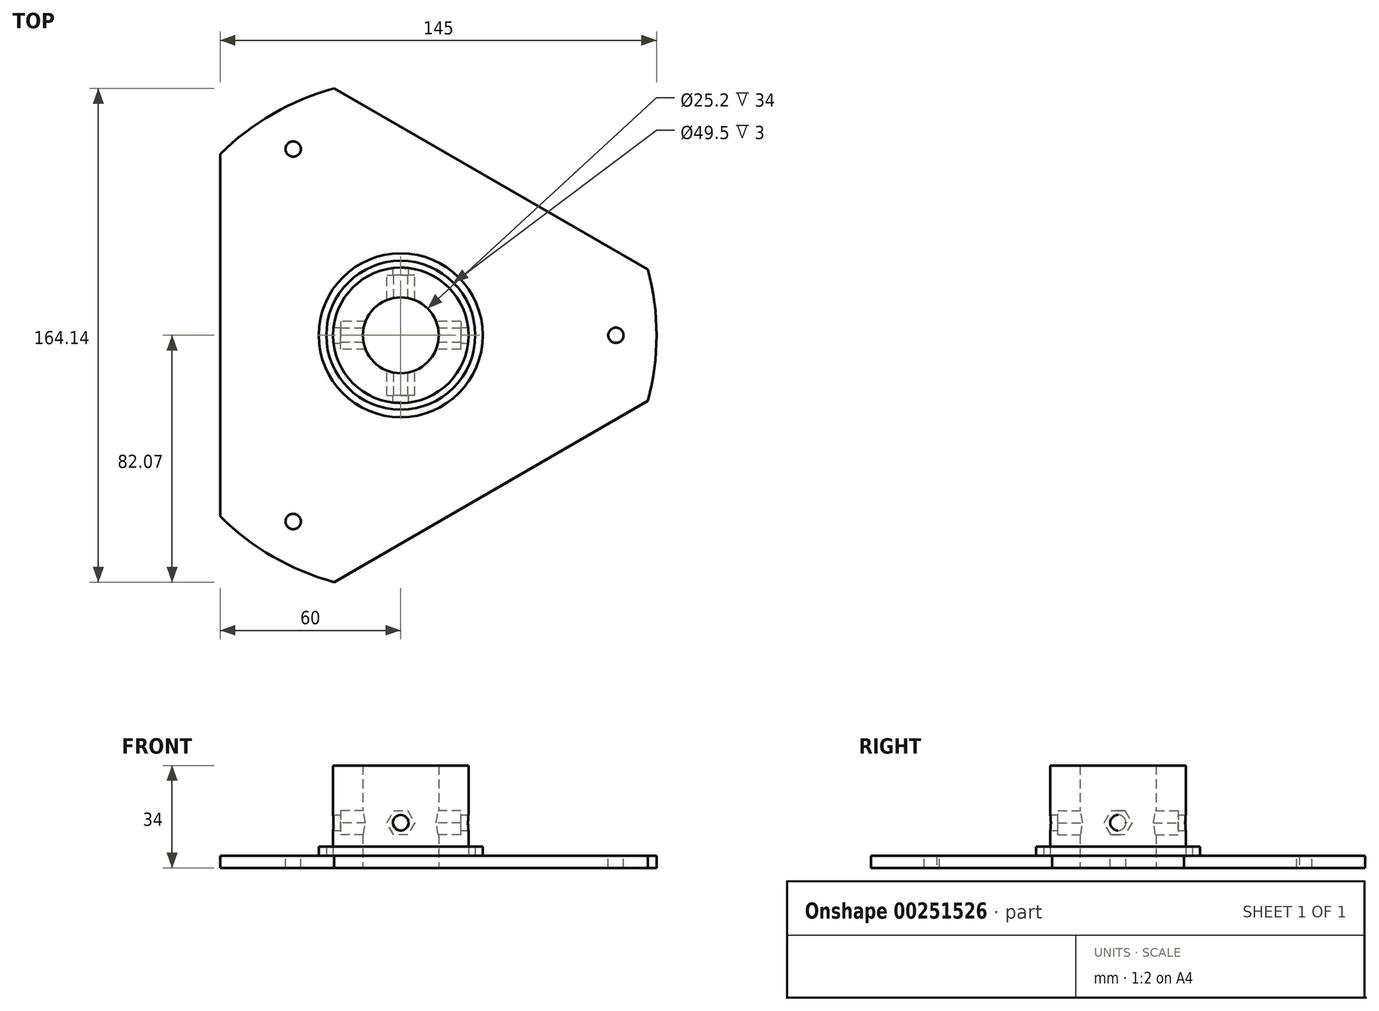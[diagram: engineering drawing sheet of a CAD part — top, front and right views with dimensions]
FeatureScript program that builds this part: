
annotation { "Feature Type Name" : "Feature", "Feature Type Description" : "" }
export const myFeature = defineFeature(function(context is Context, id is Id, definition is map)
    precondition{}
    {
        {
            var Q0;
            Q0=qCreatedBy(makeId("Top.planeOp"),FACE);
            var sketch = newSketch(context, id + "F0", { "sketchPlane" : qUnion([Q0])});
            skCircle(sketch, "E0", {"center": v(0, 0) * mm, "radius": 85 * mm});
            skCircle(sketch, "E1.cCircle", {"center": v(0, 0) * mm, "radius": 60 * mm, "construction": true});
            skLineSegment(sketch, "E1.0", {"start": v(120, 0) * mm, "end": v(-60, -103.92) * mm});
            skLineSegment(sketch, "E1.1", {"start": v(-60, -103.92) * mm, "end": v(-60, 103.92) * mm});
            skLineSegment(sketch, "E1.2", {"start": v(-60, 103.92) * mm, "end": v(120, 0) * mm});
            skPoint(sketch, "E1.0.midPoint", {"position": v(30, -51.96) * mm});
            skSolve(sketch);
        }
        {
            var Q0;
            {var subQ1=sQuery(id+"F0.wireOp",EDGE,"E0");var subQ4=sQuery(id+"F0.wireOp",EDGE,"E1.2");var subQ9=makeQuery(id+"F0.imprint","INTERSECT",VERTEX,{"disambiguationData":[OD(0.0)],"derivedFrom":[subQ1,subQ4]});Q0=makeQuery(id+"F0.imprint","IMPRINT",FACE,{"disambiguationData":[TD([[makeQuery(id+"F0.imprint","IMPRINT",EDGE,{"disambiguationData":[TD([[subQ9,-1.0]])],"derivedFrom":subQ1}),1.0]])]});}
            extrude(context, id + "F1", {"entities" : qUnion([Q0]), "depth" : 4 * mm});
        }
        {
            var Q0;
            Q0=makeQuery(id+"F1.opExtrude","CAP_FACE",FACE,{"disambiguationData":[OSD([sQuery(id+"F0.wireOp",EDGE,"E0"),sQuery(id+"F0.wireOp",EDGE,"E1.0"),sQuery(id+"F0.wireOp",EDGE,"E1.1"),sQuery(id+"F0.wireOp",EDGE,"E1.2")])],"isStart":false});
            var sketch = newSketch(context, id + "F2", { "sketchPlane" : qUnion([Q0])});
            skCircle(sketch, "E2", {"center": v(0, 0) * mm, "radius": 71.5 * mm});
            skLineSegment(sketch, "E3", {"start": v(0, 0) * mm, "end": v(118.31, 0) * mm, "construction": true});
            skCircle(sketch, "E4", {"center": v(71.5, 0) * mm, "radius": 2.55 * mm});
            skCircle(sketch, "E5.1.0", {"center": v(-35.75, 61.92) * mm, "radius": 2.55 * mm});
            skCircle(sketch, "E5.2.0", {"center": v(-35.75, -61.92) * mm, "radius": 2.55 * mm});
            skSolve(sketch);
        }
        {
            var Q0;
            {var subQ0=sQuery(id+"F2.wireOp",EDGE,"E4");var subQ1=sQuery(id+"F2.wireOp",EDGE,"E2");var subQ2=makeQuery(id+"F2.imprint","INTERSECT",VERTEX,{"disambiguationData":[OD(0.0)],"derivedFrom":[subQ1,subQ0]});Q0=makeQuery(id+"F2.imprint","IMPRINT",FACE,{"disambiguationData":[TD([[makeQuery(id+"F2.imprint","IMPRINT",EDGE,{"disambiguationData":[TD([[subQ2,1.0]])],"derivedFrom":subQ1}),1.0]])]});}
            var Q1;
            {var subQ0=sQuery(id+"F2.wireOp",EDGE,"E4");var subQ1=sQuery(id+"F2.wireOp",EDGE,"E2");var subQ2=makeQuery(id+"F2.imprint","INTERSECT",VERTEX,{"disambiguationData":[OD(0.0)],"derivedFrom":[subQ1,subQ0]});Q1=makeQuery(id+"F2.imprint","IMPRINT",FACE,{"disambiguationData":[TD([[makeQuery(id+"F2.imprint","IMPRINT",EDGE,{"disambiguationData":[TD([[subQ2,1.0]])],"derivedFrom":subQ1}),-1.0]])]});}
            var Q2;
            {var subQ0=sQuery(id+"F2.wireOp",EDGE,"E5.2.0");var subQ1=sQuery(id+"F2.wireOp",EDGE,"E2");var subQ2=makeQuery(id+"F2.imprint","INTERSECT",VERTEX,{"disambiguationData":[OD(0.0)],"derivedFrom":[subQ1,subQ0]});Q2=makeQuery(id+"F2.imprint","IMPRINT",FACE,{"disambiguationData":[TD([[makeQuery(id+"F2.imprint","IMPRINT",EDGE,{"disambiguationData":[TD([[subQ2,-1.0]])],"derivedFrom":subQ1}),-1.0]])]});}
            var Q3;
            {var subQ0=sQuery(id+"F2.wireOp",EDGE,"E5.2.0");var subQ1=sQuery(id+"F2.wireOp",EDGE,"E2");var subQ2=makeQuery(id+"F2.imprint","INTERSECT",VERTEX,{"disambiguationData":[OD(0.0)],"derivedFrom":[subQ1,subQ0]});Q3=makeQuery(id+"F2.imprint","IMPRINT",FACE,{"disambiguationData":[TD([[makeQuery(id+"F2.imprint","IMPRINT",EDGE,{"disambiguationData":[TD([[subQ2,-1.0]])],"derivedFrom":subQ1}),1.0]])]});}
            var Q4;
            {var subQ0=sQuery(id+"F2.wireOp",EDGE,"E5.1.0");var subQ1=sQuery(id+"F2.wireOp",EDGE,"E2");var subQ2=makeQuery(id+"F2.imprint","INTERSECT",VERTEX,{"disambiguationData":[OD(0.0)],"derivedFrom":[subQ1,subQ0]});Q4=makeQuery(id+"F2.imprint","IMPRINT",FACE,{"disambiguationData":[TD([[makeQuery(id+"F2.imprint","IMPRINT",EDGE,{"disambiguationData":[TD([[subQ2,-1.0]])],"derivedFrom":subQ1}),-1.0]])]});}
            var Q5;
            {var subQ0=sQuery(id+"F2.wireOp",EDGE,"E5.1.0");var subQ1=sQuery(id+"F2.wireOp",EDGE,"E2");var subQ2=makeQuery(id+"F2.imprint","INTERSECT",VERTEX,{"disambiguationData":[OD(0.0)],"derivedFrom":[subQ1,subQ0]});Q5=makeQuery(id+"F2.imprint","IMPRINT",FACE,{"disambiguationData":[TD([[makeQuery(id+"F2.imprint","IMPRINT",EDGE,{"disambiguationData":[TD([[subQ2,-1.0]])],"derivedFrom":subQ1}),1.0]])]});}
            extrude(context, id + "F3", {"entities" : qUnion([Q0, Q1, Q2, Q3, Q4, Q5]), "operationType" : NewBodyOperationType.REMOVE, "oppositeDirection" : true, "depth" : 25 * mm});
        }
        {
            var Q0;
            Q0=makeQuery(id+"F1.opExtrude","CAP_FACE",FACE,{"disambiguationData":[OSD([sQuery(id+"F0.wireOp",EDGE,"E0"),sQuery(id+"F0.wireOp",EDGE,"E1.0"),sQuery(id+"F0.wireOp",EDGE,"E1.1"),sQuery(id+"F0.wireOp",EDGE,"E1.2")])],"isStart":false});
            var sketch = newSketch(context, id + "F4", { "sketchPlane" : qUnion([Q0])});
            skCircle(sketch, "E6", {"center": v(0, 0) * mm, "radius": 12.6 * mm});
            skCircle(sketch, "E7", {"center": v(0, 0) * mm, "radius": 22.5 * mm});
            skSolve(sketch);
        }
        {
            var Q0;
            Q0=qSketchRegion(id+"F4",true);
            var Q1;
            Q1=makeQuery(id+"F4.imprint","IMPRINT",FACE,{"disambiguationData":[TD([[makeQuery(id+"F4.imprint","IMPRINT",EDGE,{"derivedFrom":sQuery(id+"F4.wireOp",EDGE,"E6")}),-1.0]])]});
            extrude(context, id + "F5", {"entities" : qUnion([Q0, Q1]), "operationType" : NewBodyOperationType.ADD, "depth" : 30 * mm});
        }
        {
            var Q0;
            Q0=makeQuery(id+"F5.boolean.opBoolean","SPLIT",FACE,{"disambiguationData":[TD([makeQuery(id+"F5.opExtrude","SWEPT_FACE",FACE,{"disambiguationData":[OSD([sQuery(id+"F4.wireOp",EDGE,"E6")])]})])],"derivedFrom":makeQuery(id+"F1.opExtrude","CAP_FACE",FACE,{"disambiguationData":[OSD([sQuery(id+"F0.wireOp",EDGE,"E0"),sQuery(id+"F0.wireOp",EDGE,"E1.0"),sQuery(id+"F0.wireOp",EDGE,"E1.1"),sQuery(id+"F0.wireOp",EDGE,"E1.2")])],"isStart":false})});
            var sketch = newSketch(context, id + "F6", { "sketchPlane" : qUnion([Q0])});
            skCircle(sketch, "E8", {"center": v(0, 0) * mm, "radius": 12.6 * mm});
            skSolve(sketch);
        }
        {
            var Q0;
            Q0=qSketchRegion(id+"F6",true);
            extrude(context, id + "F7", {"entities" : qUnion([Q0]), "operationType" : NewBodyOperationType.REMOVE, "oppositeDirection" : true, "depth" : 25 * mm});
        }
        {
            var Q0;
            Q0=qCreatedBy(makeId("Right.planeOp"),FACE);
            var sketch = newSketch(context, id + "F8", { "sketchPlane" : qUnion([Q0])});
            skLineSegment(sketch, "E9", {"start": v(0, 0) * mm, "end": v(0, 28.62) * mm, "construction": true});
            skCircle(sketch, "E10.cCircle", {"center": v(0, 15) * mm, "radius": 4 * mm, "construction": true});
            skLineSegment(sketch, "E10.0", {"start": v(2.3, 11) * mm, "end": v(-2.3, 11) * mm});
            skLineSegment(sketch, "E10.1", {"start": v(-2.3, 11) * mm, "end": v(-4.62, 15) * mm});
            skLineSegment(sketch, "E10.2", {"start": v(-4.62, 15) * mm, "end": v(-2.3, 19) * mm});
            skLineSegment(sketch, "E10.3", {"start": v(-2.3, 19) * mm, "end": v(2.3, 19) * mm});
            skLineSegment(sketch, "E10.4", {"start": v(2.3, 19) * mm, "end": v(4.62, 15) * mm});
            skLineSegment(sketch, "E10.5", {"start": v(4.62, 15) * mm, "end": v(2.3, 11) * mm});
            skPoint(sketch, "E10.0.midPoint", {"position": v(0, 11) * mm});
            skSolve(sketch);
        }
        {
            var Q0;
            Q0=qSketchRegion(id+"F8",true);
            extrude(context, id + "F9", {"entities" : qUnion([Q0]), "operationType" : NewBodyOperationType.REMOVE, "depth" : 20 * mm, "hasSecondDirection" : true, "secondDirectionOppositeDirection" : true, "secondDirectionDepth" : 20 * mm});
        }
        {
            var Q0;
            Q0=qCreatedBy(makeId("Front.planeOp"),FACE);
            var sketch = newSketch(context, id + "F10", { "sketchPlane" : qUnion([Q0])});
            skLineSegment(sketch, "E11", {"start": v(0, 0) * mm, "end": v(0, 40) * mm, "construction": true});
            skCircle(sketch, "E12.cCircle", {"center": v(0, 15) * mm, "radius": 4 * mm, "construction": true});
            skLineSegment(sketch, "E12.0", {"start": v(2.3, 11) * mm, "end": v(-2.3, 11) * mm});
            skLineSegment(sketch, "E12.1", {"start": v(-2.3, 11) * mm, "end": v(-4.62, 15) * mm});
            skLineSegment(sketch, "E12.2", {"start": v(-4.62, 15) * mm, "end": v(-2.3, 19) * mm});
            skLineSegment(sketch, "E12.3", {"start": v(-2.3, 19) * mm, "end": v(2.3, 19) * mm});
            skLineSegment(sketch, "E12.4", {"start": v(2.3, 19) * mm, "end": v(4.62, 15) * mm});
            skLineSegment(sketch, "E12.5", {"start": v(4.62, 15) * mm, "end": v(2.3, 11) * mm});
            skPoint(sketch, "E12.0.midPoint", {"position": v(0, 11) * mm});
            skSolve(sketch);
        }
        {
            var Q0;
            Q0=qSketchRegion(id+"F10",true);
            extrude(context, id + "F11", {"entities" : qUnion([Q0]), "operationType" : NewBodyOperationType.REMOVE, "depth" : 20 * mm, "hasSecondDirection" : true, "secondDirectionOppositeDirection" : true, "secondDirectionDepth" : 20 * mm});
        }
        {
            var Q0;
            Q0=qCreatedBy(makeId("Right.planeOp"),FACE);
            var sketch = newSketch(context, id + "F12", { "sketchPlane" : qUnion([Q0])});
            skLineSegment(sketch, "E13", {"start": v(0, 0) * mm, "end": v(0, 33.2) * mm});
            skCircle(sketch, "E14", {"center": v(0, 15) * mm, "radius": 2.6 * mm});
            skSolve(sketch);
        }
        {
            var Q0;
            Q0=qSketchRegion(id+"F12",true);
            extrude(context, id + "F13", {"entities" : qUnion([Q0]), "operationType" : NewBodyOperationType.REMOVE, "endBound" : BoundingType.THROUGH_ALL, "oppositeDirection" : true, "depth" : 25 * mm, "hasSecondDirection" : true, "secondDirectionBound" : SecondDirectionBoundingType.THROUGH_ALL, "secondDirectionOppositeDirection" : false, "secondDirectionDepth" : 25 * mm});
        }
        {
            var Q0;
            Q0=qCreatedBy(makeId("Front.planeOp"),FACE);
            var sketch = newSketch(context, id + "F14", { "sketchPlane" : qUnion([Q0])});
            skLineSegment(sketch, "E15", {"start": v(0, 0) * mm, "end": v(0, 19.64) * mm, "construction": true});
            skCircle(sketch, "E16", {"center": v(0, 15) * mm, "radius": 2.6 * mm});
            skSolve(sketch);
        }
        {
            var Q0;
            Q0=qSketchRegion(id+"F14",true);
            extrude(context, id + "F15", {"entities" : qUnion([Q0]), "operationType" : NewBodyOperationType.REMOVE, "endBound" : BoundingType.THROUGH_ALL, "depth" : 25 * mm, "hasSecondDirection" : true, "secondDirectionBound" : SecondDirectionBoundingType.THROUGH_ALL, "secondDirectionOppositeDirection" : true, "secondDirectionDepth" : 25 * mm});
        }
        {
            var Q0;
            {var subQ0=sQuery(id+"F0.wireOp",EDGE,"E1.0");var subQ1=sQuery(id+"F0.wireOp",EDGE,"E1.2");var subQ2=sQuery(id+"F0.wireOp",EDGE,"E0");var subQ3=sQuery(id+"F0.wireOp",EDGE,"E1.1");Q0=makeQuery(id+"F5.boolean.opBoolean","SPLIT",FACE,{"disambiguationData":[TD([makeQuery(id+"F1.opExtrude","SWEPT_FACE",FACE,{"disambiguationData":[OSD([subQ0])]})])],"derivedFrom":makeQuery(id+"F1.opExtrude","CAP_FACE",FACE,{"disambiguationData":[OSD([subQ2,subQ0,subQ3,subQ1])],"isStart":false})});}
            var sketch = newSketch(context, id + "F16", { "sketchPlane" : qUnion([Q0])});
            skCircle(sketch, "E17", {"center": v(0, 0) * mm, "radius": 27.25 * mm});
            skCircle(sketch, "E18", {"center": v(0, 0) * mm, "radius": 24.75 * mm});
            skSolve(sketch);
        }
        {
            var Q0;
            Q0 = qSketchRegion(id + "F16", true);
            extrude(context, id + "F17", {"entities" : qUnion([Q0]), "operationType" : NewBodyOperationType.ADD, "depth" : 3 * mm});
        }
    });
